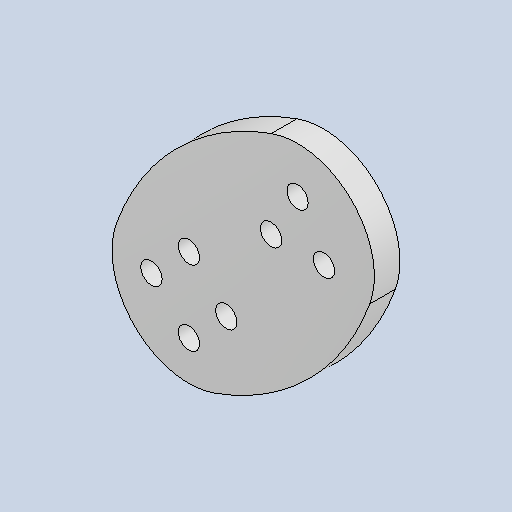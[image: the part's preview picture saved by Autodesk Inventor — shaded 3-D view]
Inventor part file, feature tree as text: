
AUTODESK INVENTOR PART (.ipt)
format: ipt  version: 2023 (Build 270158000, 158)  size: 154,624 bytes
history: native  units: mm
features: other x4, sketch x2
ambient origin geometry x8: Origin, YZ Plane, XZ Plane, XY Plane, X Axis, Y Axis, Z Axis, Center Point
bodies: Body1 (feature_tree)
feature tree (6):
  other  "駆動節.ipt"
  other  "Solid2::駆動節.ipt"
  other  "TaggingFeature1"
  sketch  "Sketch2"  dims[d0=10.0mm]
  sketch  "Sketch3"
  other  "sesaku"
